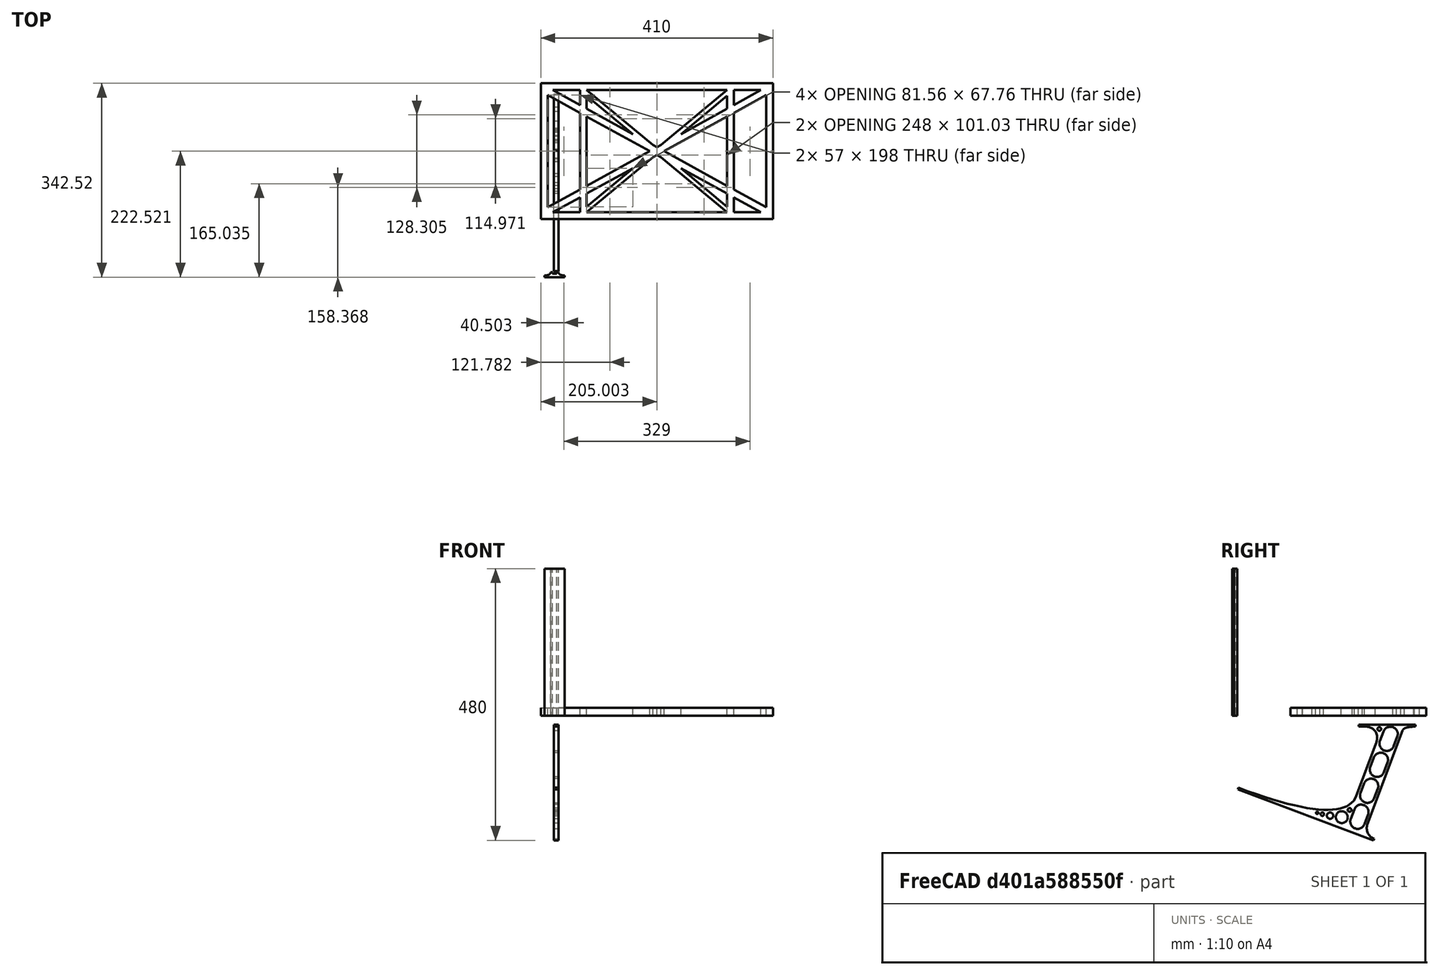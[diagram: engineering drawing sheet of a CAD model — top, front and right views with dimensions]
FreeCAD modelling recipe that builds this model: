
FCSTD DOCUMENT  (FreeCAD 0.19R0.19.2)
Label: laptopStand047
License: All rights reserved
LicenseURL: http://en.wikipedia.org/wiki/All_rights_reserved
objects: Sketcher::SketchObject×3, Part::Extrusion×3
note: 6 computed .brp shape members not serialized (recipe doc carries the construction recipe); baked Part::Feature solids carry a one-line shape summary decoded from their .brp

FEATURE [Sketcher::SketchObject] Sketch
  FullyConstrained = false
  sketch-geometry (68):
    g0: LineSegment StartX=-22.9272 StartY=136.221 StartZ=0 EndX=387.073 EndY=136.221 EndZ=0
    g1: LineSegment StartX=-22.9272 StartY=-103.779 StartZ=0 EndX=387.073 EndY=-103.779 EndZ=0
    g2: LineSegment StartX=375.073 StartY=115.221 StartZ=0 EndX=318.073 EndY=83.9235 EndZ=0
    g3: LineSegment StartX=-10.9272 StartY=-82.7794 StartZ=0 EndX=46.0728 EndY=-51.4823 EndZ=0
    g4: LineSegment StartX=-1.92719 StartY=124.221 StartZ=0 EndX=46.0728 EndY=97.8651 EndZ=0
    g5: LineSegment StartX=366.073 StartY=-91.7794 StartZ=0 EndX=318.073 EndY=-65.424 EndZ=0
    g6: LineSegment StartX=-10.9272 StartY=115.221 StartZ=0 EndX=-10.9272 EndY=-82.7794 EndZ=0
    g7: LineSegment StartX=375.073 StartY=-82.7794 StartZ=0 EndX=375.073 EndY=115.221 EndZ=0
    g8: LineSegment StartX=-1.92719 StartY=-91.7794 StartZ=0 EndX=46.0728 EndY=-91.7794 EndZ=0
    g9: LineSegment StartX=318.073 StartY=124.221 StartZ=0 EndX=366.073 EndY=124.221 EndZ=0
    g10: LineSegment StartX=306.073 StartY=-81.8102 StartZ=0 EndX=224.513 EndY=-14.0532 EndZ=0
    g11: LineSegment StartX=58.0728 StartY=114.251 StartZ=0 EndX=139.632 EndY=46.4944 EndZ=0
    g12: LineSegment StartX=306.073 StartY=124.221 StartZ=0 EndX=189.124 EndY=27.0628 EndZ=0
    g13: LineSegment StartX=58.0728 StartY=-91.7794 StartZ=0 EndX=175.022 EndY=5.37834 EndZ=0
    g14: LineSegment StartX=46.0728 StartY=124.221 StartZ=0 EndX=46.0728 EndY=97.8651 EndZ=0
    g15: LineSegment StartX=58.0728 StartY=-81.8102 StartZ=0 EndX=58.0728 EndY=-58.8351 EndZ=0
    g16: LineSegment StartX=318.073 StartY=124.221 StartZ=0 EndX=318.073 EndY=97.8651 EndZ=0
    g17: LineSegment StartX=306.073 StartY=114.251 StartZ=0 EndX=306.073 EndY=91.2763 EndZ=0
    g18: LineSegment StartX=224.513 StartY=46.4944 StartZ=0 EndX=306.073 EndY=114.251 EndZ=0
    g19: LineSegment StartX=175.022 StartY=27.0628 StartZ=0 EndX=58.0728 EndY=124.221 EndZ=0
    g20: LineSegment StartX=169.377 StartY=16.2206 StartZ=0 EndX=58.0728 EndY=77.3346 EndZ=0
    g21: LineSegment StartX=139.632 StartY=-14.0532 StartZ=0 EndX=58.0728 EndY=-81.8102 EndZ=0
    g22: LineSegment StartX=194.768 StartY=16.2206 StartZ=0 EndX=306.073 EndY=-44.8935 EndZ=0
    g23: LineSegment StartX=224.513 StartY=46.4944 StartZ=0 EndX=306.073 EndY=91.2763 EndZ=0
    g24: LineSegment StartX=175.022 StartY=27.0628 StartZ=0 EndX=179.022 EndY=24.8665 EndZ=0
    g25: LineSegment StartX=139.632 StartY=-14.0532 StartZ=0 EndX=58.0728 EndY=-58.8351 EndZ=0
    g26: LineSegment StartX=189.124 StartY=5.37834 StartZ=0 EndX=185.124 EndY=7.57463 EndZ=0
    g27: LineSegment StartX=189.124 StartY=5.37834 StartZ=0 EndX=306.073 EndY=-91.7794 EndZ=0
    g28: LineSegment StartX=306.073 StartY=77.3346 StartZ=0 EndX=306.073 EndY=-44.8935 EndZ=0
    g29: LineSegment StartX=318.073 StartY=83.9235 StartZ=0 EndX=318.073 EndY=-51.4823 EndZ=0
    g30: LineSegment StartX=318.073 StartY=97.8651 StartZ=0 EndX=366.073 EndY=124.221 EndZ=0
    g31: LineSegment StartX=306.073 StartY=77.3346 StartZ=0 EndX=194.768 EndY=16.2206 EndZ=0
    g32: LineSegment StartX=306.073 StartY=-58.8351 StartZ=0 EndX=224.513 EndY=-14.0532 EndZ=0
    g33: LineSegment StartX=306.073 StartY=-58.8351 StartZ=0 EndX=306.073 EndY=-81.8102 EndZ=0
    g34: LineSegment StartX=318.073 StartY=-51.4823 StartZ=0 EndX=375.073 EndY=-82.7794 EndZ=0
    g35: LineSegment StartX=318.073 StartY=-65.424 StartZ=0 EndX=318.073 EndY=-91.7794 EndZ=0
    g36: LineSegment StartX=306.073 StartY=124.221 StartZ=0 EndX=58.0728 EndY=124.221 EndZ=0
    g37: LineSegment StartX=318.073 StartY=-91.7794 StartZ=0 EndX=366.073 EndY=-91.7794 EndZ=0
    g38: LineSegment StartX=58.0728 StartY=-91.7794 StartZ=0 EndX=306.073 EndY=-91.7794 EndZ=0
    g39: LineSegment StartX=58.0728 StartY=-44.8935 StartZ=0 EndX=58.0728 EndY=77.3346 EndZ=0
    g40: LineSegment StartX=46.0728 StartY=-65.424 StartZ=0 EndX=-1.92719 EndY=-91.7794 EndZ=0
    g41: LineSegment StartX=46.0728 StartY=-65.424 StartZ=0 EndX=46.0728 EndY=-91.7794 EndZ=0
    g42: LineSegment StartX=58.0728 StartY=-44.8935 StartZ=0 EndX=169.377 EndY=16.2206 EndZ=0
    g43: LineSegment StartX=58.0728 StartY=91.2763 StartZ=0 EndX=58.0728 EndY=114.251 EndZ=0
    g44: LineSegment StartX=46.0728 StartY=83.9235 StartZ=0 EndX=46.0728 EndY=-51.4823 EndZ=0
    g45: LineSegment StartX=46.0728 StartY=124.221 StartZ=0 EndX=-1.92719 EndY=124.221 EndZ=0
    g46: LineSegment StartX=58.0728 StartY=91.2763 StartZ=0 EndX=139.632 EndY=46.4944 EndZ=0
    g47: LineSegment StartX=46.0728 StartY=83.9235 StartZ=0 EndX=-10.9272 EndY=115.221 EndZ=0
    g48: LineSegment StartX=-22.9272 StartY=136.221 StartZ=0 EndX=-42.9272 EndY=136.221 EndZ=0
    g49: LineSegment StartX=387.073 StartY=136.221 StartZ=0 EndX=407.073 EndY=136.221 EndZ=0
    g50: LineSegment StartX=-42.9272 StartY=136.221 StartZ=0 EndX=-42.9272 EndY=-103.779 EndZ=0
    g51: LineSegment StartX=-22.9272 StartY=-103.779 StartZ=0 EndX=-42.9272 EndY=-103.779 EndZ=0
    g52: LineSegment StartX=407.073 StartY=136.221 StartZ=0 EndX=407.073 EndY=-103.779 EndZ=0
    g53: LineSegment StartX=387.073 StartY=-103.779 StartZ=0 EndX=407.073 EndY=-103.779 EndZ=0
    g54: LineSegment StartX=179.022 StartY=27.0628 StartZ=0 EndX=179.022 EndY=124.221 EndZ=0
    g55: LineSegment StartX=185.124 StartY=27.0628 StartZ=0 EndX=185.124 EndY=124.221 EndZ=0
    g56: LineSegment StartX=179.022 StartY=27.0628 StartZ=0 EndX=179.022 EndY=24.8665 EndZ=0
    g57: LineSegment StartX=185.124 StartY=27.0628 StartZ=0 EndX=185.124 EndY=24.8665 EndZ=0
    g58: LineSegment StartX=185.124 StartY=7.57463 StartZ=0 EndX=185.124 EndY=-91.7794 EndZ=0
    g59: LineSegment StartX=179.022 StartY=7.57463 StartZ=0 EndX=179.022 EndY=-91.7794 EndZ=0
    g60: LineSegment StartX=189.124 StartY=27.0628 StartZ=0 EndX=185.124 EndY=24.8665 EndZ=0
    g61: LineSegment StartX=175.022 StartY=5.37834 StartZ=0 EndX=179.022 EndY=7.57463 EndZ=0
    g62: ArcOfCircle CenterX=-26.9272 CenterY=22.1087 CenterZ=0 NormalX=0 NormalY=0 NormalZ=1 AngleXU=0 Radius=8 StartAngle=1e-16 EndAngle=3.14159
    g63: ArcOfCircle CenterX=-26.9272 CenterY=-83.7794 CenterZ=0 NormalX=0 NormalY=0 NormalZ=1 AngleXU=0 Radius=8 StartAngle=3.14159 EndAngle=6.28319
    g64: LineSegment StartX=-34.9272 StartY=22.1087 StartZ=0 EndX=-34.9272 EndY=-83.7794 EndZ=0
    g65: LineSegment StartX=-18.9272 StartY=22.1087 StartZ=0 EndX=-18.9272 EndY=-83.7794 EndZ=0
    g66: LineSegment StartX=407.073 StartY=-91.7794 StartZ=0 EndX=391.073 EndY=-91.7794 EndZ=0
    g67: LineSegment StartX=391.073 StartY=-91.7794 StartZ=0 EndX=391.073 EndY=-83.7794 EndZ=0
  constraints (139):
    c: Horizontal(g0)
    c: Distance(g0) = 410
    c: Horizontal(g1)
    c: Block(g0)
    c: Horizontal(g8)
    c: Horizontal(g9)
    c: Tangent(g5,g20)
    c: PointOnObject(g20,g3)
    c: PointOnObject(g22,g2)
    c: Coincident(g46,g11)
    c: Coincident(g24,g19)
    c: Coincident(g18,g23)
    c: Coincident(g25,g21)
    c: Coincident(g32,g10)
    c: Coincident(g27,g26)
    c: Coincident(g18,g17)
    c: Tangent(g17,g28)
    c: Tangent(g16,g29)
    c: Coincident(g23,g17)
    c: Tangent(g23,g30)
    c: Coincident(g2,g29)
    c: Coincident(g31,g28)
    c: Tangent(g2,g31)
    c: Coincident(g33,g10)
    c: Tangent(g5,g32)
    c: Tangent(g28,g33)
    c: Coincident(g22,g28)
    c: Tangent(g22,g34)
    c: Coincident(g29,g34)
    c: Coincident(g35,g5)
    c: Tangent(g29,g35)
    c: Coincident(g21,g15)
    c: Tangent(g15,g39)
    c: Coincident(g25,g15)
    c: Tangent(g25,g40)
    c: Coincident(g41,g40)
    c: Tangent(g14,g41)
    c: Coincident(g3,g44)
    c: Coincident(g42,g39)
    c: Tangent(g3,g42)
    c: Tangent(g39,g43)
    c: Tangent(g14,g44)
    c: Coincident(g11,g43)
    c: PointOnObject(g36,g19)
    c: Tangent(g36,g45)
    c: Coincident(g4,g14)
    c: Coincident(g46,g43)
    c: Tangent(g4,g46)
    c: Coincident(g20,g39)
    c: Coincident(g47,g44)
    c: Tangent(g20,g47)
    c: Block(g19)
    c: Block(g12)
    c: Block(g36)
    c: Block(g16)
    c: Block(g30)
    c: Block(g2)
    c: Block(g34)
    c: Block(g7)
    c: Block(g32)
    c: Block(g33)
    c: Block(g5)
    c: Block(g35)
    c: Block(g18)
    c: Block(g27)
    c: Block(g38)
    c: Block(g13)
    c: Block(g25)
    c: Block(g21)
    c: Block(g41)
    c: Block(g40)
    c: Block(g3)
    c: Block(g6)
    c: Block(g47)
    c: Block(g4)
    c: Block(g14)
    c: Block(g11)
    c: Block(g43)
    c: Block(g31)
    c: Block(g28)
    c: Block(g20)
    c: Block(g42)
    c: Block(g45)
    c: Block(g9)
    c: Block(g37)
    c: Block(g8)
    c: Horizontal(g48)
    c: Distance(g48) = 20
    c: Coincident(g49,g0)
    c: Horizontal(g49)
    c: Distance(g49) = 20
    c: Coincident(g50,g48)
    c: Vertical(g50)
    c: Horizontal(g51)
    c: Coincident(g51,g50)
    c: Coincident(g52,g49)
    c: Vertical(g52)
    c: Coincident(g53,g1)
    c: Horizontal(g53)
    c: Coincident(g53,g52)
    c: Block(g52)
    c: Block(g51)
    c: Block(g50)
    c: Block(g1)
    c: Vertical(g54)
    c: Vertical(g55)
    c: Vertical(g56)
    c: Vertical(g57)
    c: PointOnObject(g55,g36)
    c: PointOnObject(g54,g36)
    c: Tangent(g57,g58)
    c: PointOnObject(g58,g38)
    c: PointOnObject(g59,g38)
    c: Tangent(g56,g59)
    c: Coincident(g24,g56)
    c: Coincident(g26,g58)
    c: Block(g54)
    c: Block(g55)
    c: Block(g59)
    c: Block(g58)
    c: Coincident(g60,g12)
    c: Coincident(g60,g57)
    c: Coincident(g61,g13)
    c: Coincident(g61,g59)
    c: Tangent(g62,g65) = 1.5708
    c: Tangent(g62,g64) = -1.5708
    c: Tangent(g64,g63) = -1.5708
    c: Tangent(g65,g63) = 1.5708
    c: Vertical(g64)
    c: Equal(g62,g63)
    c: Block(g65)
    c: Block(g64)
    c: PointOnObject(g66,g52)
    c: Horizontal(g66)
    c: Distance(g66) = 16
    c: Block(g66)
    c: Coincident(g67,g66)
    c: Vertical(g67)
    c: Distance(g67) = 8
FEATURE [Sketcher::SketchObject] Sketch001
  FullyConstrained = true
  MapMode = 4
  Placement = pos=(0,0,0) rot=(0.57735,0.57735,0.57735;2.0944rad)
  Support = -> [Sketch]
  sketch-geometry (46):
    g0: BSplineCurve PolesCount=3 KnotsCount=2 Degree=2 IsPeriodic=0
    g1: ArcOfCircle CenterX=73.122 CenterY=-32.2909 CenterZ=0 NormalX=0 NormalY=0 NormalZ=1 AngleXU=0 Radius=13 StartAngle=5.92268 EndAngle=9.06428
    g2: ArcOfCircle CenterX=66.7816 CenterY=-49.1439 CenterZ=0 NormalX=0 NormalY=0 NormalZ=1 AngleXU=0 Radius=13 StartAngle=2.78068 EndAngle=5.92131
    g3: ArcOfCircle CenterX=55.9263 CenterY=-78.1807 CenterZ=0 NormalX=0 NormalY=0 NormalZ=1 AngleXU=0 Radius=13 StartAngle=5.92268 EndAngle=9.06428
    g4: ArcOfCircle CenterX=49.5884 CenterY=-95.0342 CenterZ=0 NormalX=0 NormalY=0 NormalZ=1 AngleXU=0 Radius=13 StartAngle=2.78068 EndAngle=5.92131
    g5: ArcOfCircle CenterX=38.7206 CenterY=-124.067 CenterZ=0 NormalX=0 NormalY=0 NormalZ=1 AngleXU=0 Radius=13 StartAngle=5.92268 EndAngle=9.06428
    g6: ArcOfCircle CenterX=32.3875 CenterY=-140.92 CenterZ=0 NormalX=0 NormalY=0 NormalZ=1 AngleXU=0 Radius=13 StartAngle=2.78068 EndAngle=5.92131
    g7: ArcOfCircle CenterX=21.4715 CenterY=-169.934 CenterZ=0 NormalX=0 NormalY=0 NormalZ=1 AngleXU=0 Radius=13 StartAngle=5.92268 EndAngle=9.06428
    g8: ArcOfCircle CenterX=15.1336 CenterY=-186.787 CenterZ=0 NormalX=0 NormalY=0 NormalZ=1 AngleXU=0 Radius=13 StartAngle=2.78068 EndAngle=5.92131
    g9-g12: Circle x4 (B-spline internal-alignment scaffolding for g13; pole/knot coordinates omitted)
    g13: BSplineCurve PolesCount=4 KnotsCount=2 Degree=3 IsPeriodic=0
    g14: GeomPoint X=28.8094 Y=-19.0875 Z=0
    g15: GeomPoint X=47.0443 Y=-50.4712 Z=0
    g16: Circle CenterX=53.5586 CenterY=-23.2695 CenterZ=0 NormalX=0 NormalY=0 NormalZ=1 AngleXU=0 Radius=3.24518
    g17: Circle CenterX=-195.441 CenterY=-127.082 CenterZ=0 NormalX=0 NormalY=0 NormalZ=1 AngleXU=0 Radius=1
    g18: Circle CenterX=-8.24091 CenterY=-197.481 CenterZ=0 NormalX=0 NormalY=0 NormalZ=1 AngleXU=0 Radius=1
    g19: Circle CenterX=12.8789 CenterY=-141.321 CenterZ=0 NormalX=0 NormalY=0 NormalZ=1 AngleXU=0 Radius=1
    g20: BSplineCurve PolesCount=3 KnotsCount=2 Degree=2 IsPeriodic=0
    g21: GeomPoint X=-195.441 Y=-127.082 Z=0
    g22: GeomPoint X=12.8789 Y=-141.321 Z=0
    g23: Circle CenterX=-12.8016 CenterY=-179.036 CenterZ=0 NormalX=0 NormalY=0 NormalZ=1 AngleXU=0 Radius=10.5072
    g24: Circle CenterX=0.933922 CenterY=-166.43 CenterZ=0 NormalX=0 NormalY=0 NormalZ=1 AngleXU=0 Radius=3.26661
    g25: Circle CenterX=-33.5518 CenterY=-176.44 CenterZ=0 NormalX=0 NormalY=0 NormalZ=1 AngleXU=0 Radius=5.64388
    g26: Circle CenterX=-47.2366 CenterY=-173.859 CenterZ=0 NormalX=0 NormalY=0 NormalZ=1 AngleXU=0 Radius=3.01653
    g27: Circle CenterX=-56.2595 CenterY=-171.456 CenterZ=0 NormalX=0 NormalY=0 NormalZ=1 AngleXU=0 Radius=2.12826
    g28: ArcOfCircle CenterX=51.2151 CenterY=-198.473 CenterZ=0 NormalX=0 NormalY=0 NormalZ=1 AngleXU=0 Radius=20 StartAngle=2.78189 EndAngle=4.35269
    g29: LineSegment StartX=32.4951 StartY=-191.433 StartZ=0 EndX=94.6577 EndY=-26.1351 EndZ=0
    g30: LineSegment StartX=43.1192 StartY=-220.001 StartZ=0 EndX=-196.497 EndY=-129.89 EndZ=0
    g31: LineSegment StartX=43.1192 StartY=-220.001 StartZ=0 EndX=44.1752 EndY=-217.193 EndZ=0
    g32: LineSegment StartX=117.223 StartY=-19.0875 StartZ=0 EndX=117.223 EndY=-16.0875 EndZ=0
    g33: LineSegment StartX=117.223 StartY=-16.0875 StartZ=0 EndX=17.2232 EndY=-16.0875 EndZ=0
    g34: LineSegment StartX=17.2232 StartY=-16.0875 StartZ=0 EndX=17.2232 EndY=-19.0875 EndZ=0
    g35: LineSegment StartX=28.8094 StartY=-19.0875 StartZ=0 EndX=17.2232 EndY=-19.0875 EndZ=0
    g36: LineSegment StartX=47.0443 StartY=-50.4712 StartZ=0 EndX=12.8789 EndY=-141.321 EndZ=0
    g37: LineSegment StartX=-195.441 StartY=-127.082 StartZ=0 EndX=-196.497 EndY=-129.89 EndZ=0
    g38: LineSegment StartX=85.2864 StartY=-36.8765 StartZ=0 EndX=78.9396 EndY=-53.7463 EndZ=0
    g39: LineSegment StartX=60.9577 StartY=-27.7052 StartZ=0 EndX=54.6191 EndY=-44.5532 EndZ=0
    g40: LineSegment StartX=68.0907 StartY=-82.7664 StartZ=0 EndX=61.7465 EndY=-99.6365 EndZ=0
    g41: LineSegment StartX=43.7619 StartY=-73.595 StartZ=0 EndX=37.426 EndY=-90.4435 EndZ=0
    g42: LineSegment StartX=50.885 StartY=-128.652 StartZ=0 EndX=44.5456 EndY=-145.522 EndZ=0
    g43: LineSegment StartX=26.5562 StartY=-119.481 StartZ=0 EndX=20.2251 EndY=-136.329 EndZ=0
    g44: LineSegment StartX=9.3071 StartY=-165.349 StartZ=0 EndX=2.97115 EndY=-182.197 EndZ=0
    g45: LineSegment StartX=33.6358 StartY=-174.52 StartZ=0 EndX=27.2917 EndY=-191.39 EndZ=0
  constraints (70):
    c: Block(g0)
    c: Block(g1)
    c: Block(g2)
    c: Block(g4)
    c: Block(g3)
    c: Block(g6)
    c: Block(g5)
    c: Block(g8)
    c: Block(g7)
    c: Weight(g9) = 1
    c: Equal(g9,g10)
    c: Equal(g9,g11)
    c: Equal(g9,g12)
    c: InternalAlignment(g9-g12 -> g13) x4
    c: InternalAlignment(g14,g13)
    c: InternalAlignment(g15,g13)
    c: Block(g16)
    c: Weight(g17) = 1
    c: Equal(g17,g18)
    c: Equal(g17,g19)
    c: InternalAlignment(g17,g20)
    c: InternalAlignment(g18,g20)
    c: InternalAlignment(g19,g20)
    c: InternalAlignment(g21,g20)
    c: InternalAlignment(g22,g20)
    c: Block(g20)
    c: Block(g23)
    c: Block(g24)
    c: Block(g25)
    c: Block(g26)
    c: Block(g27)
    c: Block(g28)
    c: Coincident(g29,g28)
    c: Coincident(g29,g0)
    c: Block(g13)
    c: Coincident(g31,g30)
    c: Coincident(g31,g28)
    c: Block(g31)
    c: Coincident(g32,g0)
    c: Vertical(g32)
    c: Coincident(g33,g32)
    c: Horizontal(g33)
    c: Coincident(g34,g33)
    c: Vertical(g34)
    c: Block(g33)
    c: Coincident(g35,g13)
    c: Coincident(g35,g34)
    c: Horizontal(g35)
    c: Coincident(g36,g13)
    c: Coincident(g36,g20)
    c: Coincident(g37,g20)
    c: Coincident(g37,g30)
    c: Block(g30)
    c: Coincident(g38,g1)
    c: Coincident(g38,g2)
    c: Coincident(g39,g1)
    c: Coincident(g39,g2)
    c: Coincident(g40,g3)
    c: Coincident(g40,g4)
    c: Coincident(g41,g3)
    c: Coincident(g41,g4)
    c: Coincident(g42,g5)
    c: Coincident(g42,g6)
    c: Coincident(g43,g5)
    c: Coincident(g43,g6)
    c: Coincident(g44,g7)
    c: Coincident(g44,g8)
    c: Coincident(g45,g7)
    c: Coincident(g45,g8)
    c: Distance(g30) = 256
FEATURE [Part::Extrusion] Extrude002
  Base = -> Sketch001
  Dir = (1,0,0)
  DirMode = 2
  FaceMakerClass = Part::FaceMakerBullseye
  LengthFwd = 8
  LengthRev = 0
  Solid = true
  Symmetric = false
FEATURE [Sketcher::SketchObject] Sketch002
  FullyConstrained = true
  sketch-geometry (20):
    g0: LineSegment StartX=-2.77179 StartY=-200.304 StartZ=0 EndX=5.22821 EndY=-200.304 EndZ=0
    g1: LineSegment StartX=5.22821 StartY=-200.304 StartZ=0 EndX=5.22821 EndY=-197.304 EndZ=0
    g2: LineSegment StartX=-2.77179 StartY=-200.304 StartZ=0 EndX=-2.77179 EndY=-197.304 EndZ=0
    g3: LineSegment StartX=5.22821 StartY=-197.304 StartZ=0 EndX=8.22821 EndY=-197.304 EndZ=0
    g4: LineSegment StartX=-2.77179 StartY=-197.304 StartZ=0 EndX=-5.77179 EndY=-197.304 EndZ=0
    g5: LineSegment StartX=19.2282 StartY=-203.304 StartZ=0 EndX=19.2282 EndY=-206.304 EndZ=0
    g6: LineSegment StartX=-16.7718 StartY=-203.304 StartZ=0 EndX=-16.7718 EndY=-206.304 EndZ=0
    g7: LineSegment StartX=-16.7718 StartY=-206.304 StartZ=0 EndX=19.2282 EndY=-206.304 EndZ=0
    g8: Circle CenterX=-16.7718 CenterY=-203.304 CenterZ=0 NormalX=0 NormalY=0 NormalZ=1 AngleXU=0 Radius=1
    g9: Circle CenterX=-5.77179 CenterY=-203.304 CenterZ=0 NormalX=0 NormalY=0 NormalZ=1 AngleXU=0 Radius=1
    g10: Circle CenterX=-5.77179 CenterY=-197.304 CenterZ=0 NormalX=0 NormalY=0 NormalZ=1 AngleXU=0 Radius=1
    g11: BSplineCurve PolesCount=3 KnotsCount=2 Degree=2 IsPeriodic=0
    g12: GeomPoint X=-16.7718 Y=-203.304 Z=0
    g13: GeomPoint X=-5.77179 Y=-197.304 Z=0
    g14: Circle CenterX=19.2282 CenterY=-203.304 CenterZ=0 NormalX=0 NormalY=0 NormalZ=1 AngleXU=0 Radius=1
    g15: Circle CenterX=8.22821 CenterY=-203.304 CenterZ=0 NormalX=0 NormalY=0 NormalZ=1 AngleXU=0 Radius=1
    g16: Circle CenterX=8.22821 CenterY=-197.304 CenterZ=0 NormalX=0 NormalY=0 NormalZ=1 AngleXU=0 Radius=1
    g17: BSplineCurve PolesCount=3 KnotsCount=2 Degree=2 IsPeriodic=0
    g18: GeomPoint X=19.2282 Y=-203.304 Z=0
    g19: GeomPoint X=8.22821 Y=-197.304 Z=0
  constraints (41):
    c: Horizontal(g0)
    c: Distance(g0) = 8
    c: Coincident(g1,g0)
    c: Vertical(g1)
    c: Distance(g1) = 3
    c: Coincident(g2,g0)
    c: Vertical(g2)
    c: Distance(g2) = 3
    c: Coincident(g3,g1)
    c: Horizontal(g3)
    c: Distance(g3) = 3
    c: Coincident(g4,g2)
    c: Horizontal(g4)
    c: Distance(g4) = 3
    c: Vertical(g5)
    c: Vertical(g6)
    c: Coincident(g7,g6)
    c: Coincident(g7,g5)
    c: Weight(g8) = 1
    c: Equal(g8,g9)
    c: Equal(g8,g10)
    c: Coincident(g11,g4)
    c: InternalAlignment(g8,g11)
    c: InternalAlignment(g9,g11)
    c: InternalAlignment(g10,g11)
    c: InternalAlignment(g12,g11)
    c: InternalAlignment(g13,g11)
    c: Coincident(g17,g5)
    c: Weight(g14) = 1
    c: Equal(g14,g15)
    c: Equal(g14,g16)
    c: Coincident(g17,g3)
    c: InternalAlignment(g14,g17)
    c: InternalAlignment(g15,g17)
    c: InternalAlignment(g16,g17)
    c: InternalAlignment(g18,g17)
    c: InternalAlignment(g19,g17)
    c: Block(g7)
    c: Block(g17)
    c: Block(g11)
    c: Block(g6)
FEATURE [Part::Extrusion] Extrude003
  Base = -> Sketch002
  Dir = (0,0,1)
  DirMode = 2
  FaceMakerClass = Part::FaceMakerBullseye
  LengthFwd = 260
  LengthRev = 0
  Solid = true
  Symmetric = false
FEATURE [Part::Extrusion] Extrude
  Base = -> Sketch
  Dir = (0,0,1)
  DirMode = 2
  FaceMakerClass = Part::FaceMakerBullseye
  LengthFwd = 14
  LengthRev = 0
  Solid = true
  Symmetric = false
